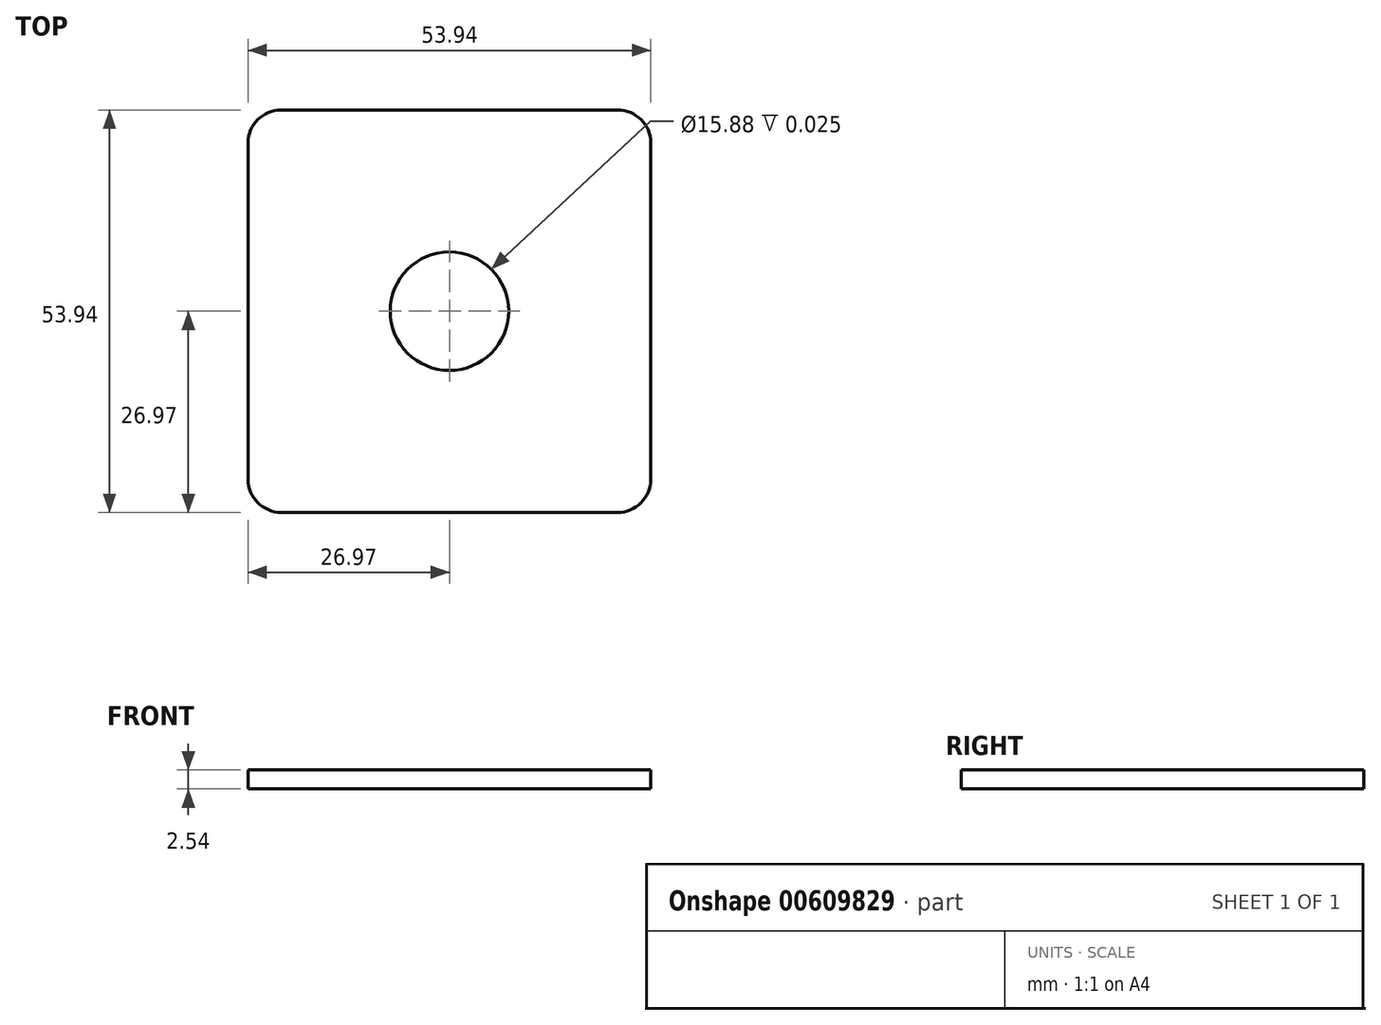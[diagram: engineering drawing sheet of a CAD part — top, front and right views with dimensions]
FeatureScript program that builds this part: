
annotation { "Feature Type Name" : "Feature", "Feature Type Description" : "" }
export const myFeature = defineFeature(function(context is Context, id is Id, definition is map)
    precondition{}
    {
        {
            var Q0;
            Q0=qCreatedBy(makeId("Top.planeOp"),FACE);
            var sketch = newSketch(context, id + "F0", { "sketchPlane" : qUnion([Q0])});
            skLineSegment(sketch, "E0.bottom", {"start": v(-22.52, 26.97) * mm, "end": v(22.52, 26.97) * mm});
            skLineSegment(sketch, "E0.top", {"start": v(-22.52, -26.97) * mm, "end": v(22.52, -26.97) * mm});
            skLineSegment(sketch, "E0.left", {"start": v(-26.97, 22.52) * mm, "end": v(-26.97, -22.52) * mm});
            skLineSegment(sketch, "E0.right", {"start": v(26.97, 22.52) * mm, "end": v(26.97, -22.52) * mm});
            skPoint(sketch, "E0.middle", {"position": v(0, 0) * mm});
            skPoint(sketch, "E1.visualSharp", {"position": v(-26.97, 26.97) * mm});
            skArc(sketch, "E1.filletArc", {"start": v(-22.52, 26.97) * mm, "mid": v(-25.67, 25.67) * mm, "end": v(-26.97, 22.52) * mm});
            skPoint(sketch, "E2.visualSharp", {"position": v(-26.97, -26.97) * mm});
            skArc(sketch, "E2.filletArc", {"start": v(-26.97, -22.52) * mm, "mid": v(-25.67, -25.67) * mm, "end": v(-22.52, -26.97) * mm});
            skPoint(sketch, "E3.visualSharp", {"position": v(26.97, -26.97) * mm});
            skArc(sketch, "E3.filletArc", {"start": v(22.52, -26.97) * mm, "mid": v(25.67, -25.67) * mm, "end": v(26.97, -22.52) * mm});
            skPoint(sketch, "E4.visualSharp", {"position": v(26.97, 26.97) * mm});
            skArc(sketch, "E4.filletArc", {"start": v(26.97, 22.52) * mm, "mid": v(25.67, 25.67) * mm, "end": v(22.52, 26.97) * mm});
            skSolve(sketch);
        }
        {
            var Q0;
            Q0 = qSketchRegion(id + "F0", true);
            extrude(context, id + "F1", {"entities" : qUnion([Q0]), "depth" : 2.54 * mm, "offsetDistance" : 25.4 * mm});
        }
        {
            var Q0;
            Q0=makeQuery(id+"F1.opExtrude","CAP_FACE",FACE,{"disambiguationData":[OSD([sQuery(id+"F0.wireOp",EDGE,"E0.bottom"),sQuery(id+"F0.wireOp",EDGE,"E0.top"),sQuery(id+"F0.wireOp",EDGE,"E0.left"),sQuery(id+"F0.wireOp",EDGE,"E0.right"),sQuery(id+"F0.wireOp",EDGE,"E1.filletArc"),sQuery(id+"F0.wireOp",EDGE,"E2.filletArc"),sQuery(id+"F0.wireOp",EDGE,"E3.filletArc"),sQuery(id+"F0.wireOp",EDGE,"E4.filletArc")])],"isStart":false});
            var sketch = newSketch(context, id + "F2", { "sketchPlane" : qUnion([Q0])});
            skCircle(sketch, "E5", {"center": v(0, 0) * mm, "radius": 7.94 * mm});
            skSolve(sketch);
        }
        {
            var Q0;
            Q0 = qSketchRegion(id + "F2", true);
            extrude(context, id + "F3", {"entities" : qUnion([Q0]), "operationType" : NewBodyOperationType.REMOVE, "oppositeDirection" : true, "depth" : 0.03 * mm, "offsetDistance" : 25.4 * mm});
        }
    });
